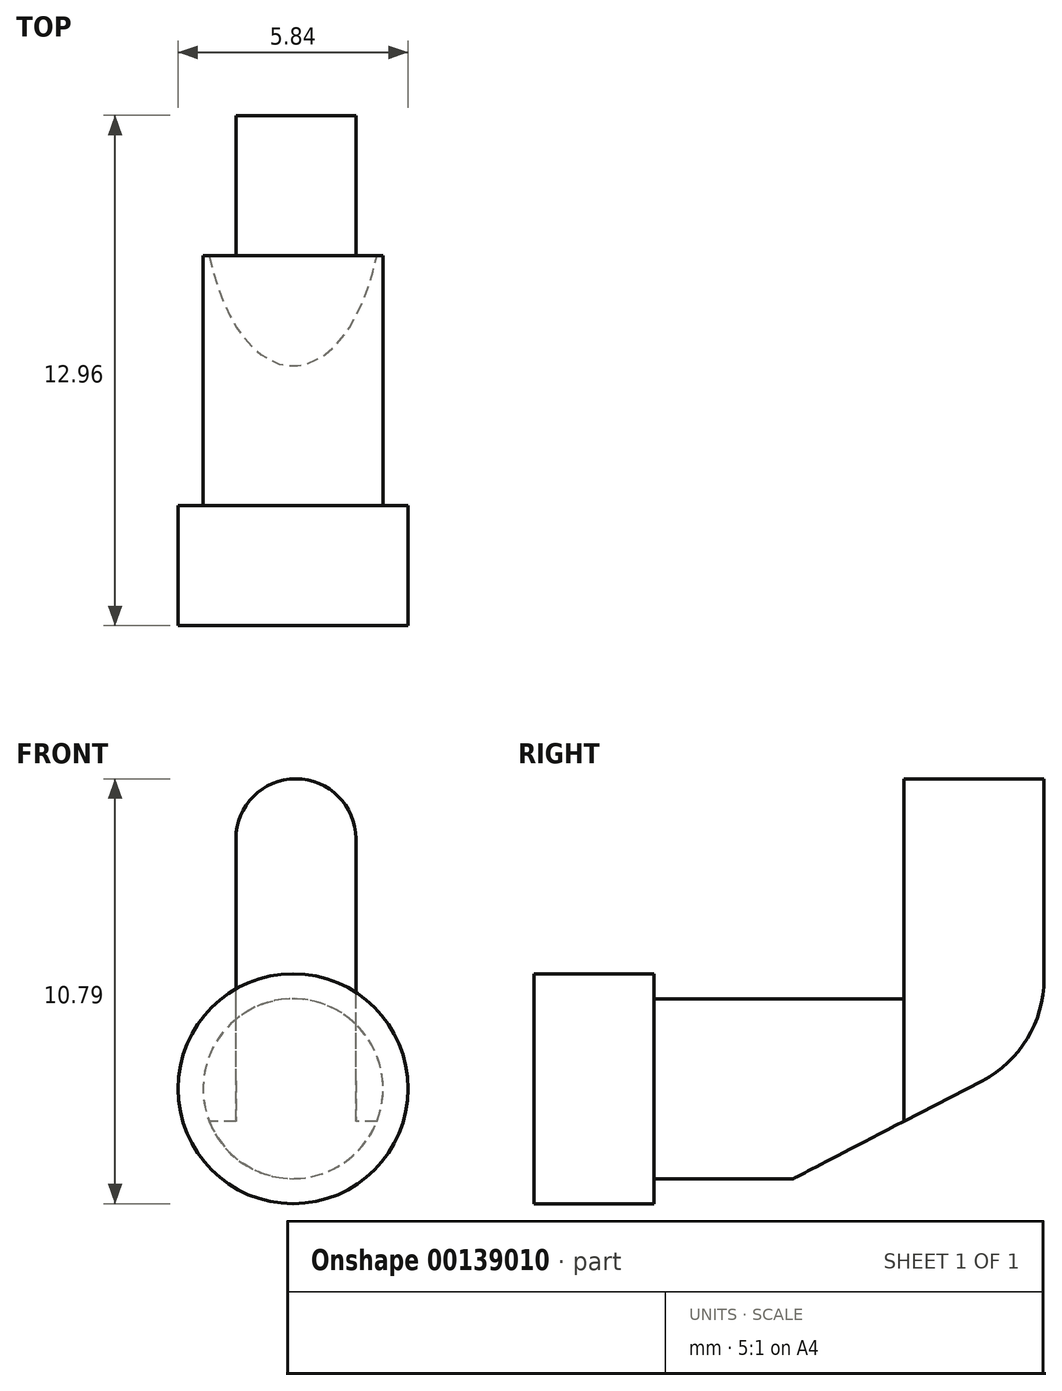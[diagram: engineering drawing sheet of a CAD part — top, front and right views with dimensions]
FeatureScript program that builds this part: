
annotation { "Feature Type Name" : "Feature", "Feature Type Description" : "" }
export const myFeature = defineFeature(function(context is Context, id is Id, definition is map)
    precondition{}
    {
        {
            var Q0;
            Q0=qCreatedBy(makeId("Front.planeOp"),FACE);
            var sketch = newSketch(context, id + "F0", { "sketchPlane" : qUnion([Q0])});
            skCircle(sketch, "E0", {"center": v(0, 0) * mm, "radius": 2.29 * mm});
            skSolve(sketch);
        }
        {
            var Q0;
            Q0 = qSketchRegion(id + "F0", true);
            extrude(context, id + "F1", {"entities" : qUnion([Q0]), "depth" : 6.35 * mm});
        }
        {
            var Q0;
            Q0=makeQuery(id+"F1.opExtrude","CAP_FACE",FACE,{"disambiguationData":[OSD([sQuery(id+"F0.wireOp",EDGE,"E0")])],"isStart":false});
            var sketch = newSketch(context, id + "F2", { "sketchPlane" : qUnion([Q0])});
            skCircle(sketch, "E1", {"center": v(0, 0) * mm, "radius": 2.92 * mm});
            skSolve(sketch);
        }
        {
            var Q0;
            Q0 = qSketchRegion(id + "F2", true);
            extrude(context, id + "F3", {"entities" : qUnion([Q0]), "operationType" : NewBodyOperationType.ADD, "depth" : 3.05 * mm});
        }
        {
            var Q0;
            Q0=makeQuery(id+"F1.opExtrude","CAP_FACE",FACE,{"disambiguationData":[OSD([sQuery(id+"F0.wireOp",EDGE,"E0")])],"isStart":true});
            var sketch = newSketch(context, id + "F4", { "sketchPlane" : qUnion([Q0])});
            skLineSegment(sketch, "E2", {"start": v(-1.6, 0) * mm, "end": v(-1.6, 6.36) * mm});
            skLineSegment(sketch, "E3", {"start": v(1.45, 0) * mm, "end": v(1.45, 6.35) * mm});
            skLineSegment(sketch, "E4", {"start": v(-1.6, 0) * mm, "end": v(1.45, 0) * mm});
            skArc(sketch, "E5", {"start": v(1.45, 6.35) * mm, "mid": v(-0.07, 7.87) * mm, "end": v(-1.6, 6.36) * mm});
            skSolve(sketch);
        }
        {
            var Q0;
            Q0 = qSketchRegion(id + "F4", true);
            extrude(context, id + "F5", {"entities" : qUnion([Q0]), "operationType" : NewBodyOperationType.ADD, "depth" : 3.56 * mm});
        }
        {
            var Q0;
            Q0=makeQuery(id+"F5.opExtrude","SWEPT_FACE",FACE,{"disambiguationData":[OSD([sQuery(id+"F4.wireOp",EDGE,"E2")])]});
            var sketch = newSketch(context, id + "F6", { "sketchPlane" : qUnion([Q0])});
            skFitSpline(sketch, "E6", {"points": [v(3.56, 0) * mm, v(0, -1.3) * mm], "startDerivative": vector(0.31, -3.55) * mm, "endDerivative": vector(-10.98, -0.34) * mm});
            skLineSegment(sketch, "E7", {"start": v(0, -1.3) * mm, "end": v(0, 0) * mm});
            skLineSegment(sketch, "E8", {"start": v(0, 0) * mm, "end": v(3.56, 0) * mm});
            skSolve(sketch);
        }
        {
            var Q0;
            Q0=makeQuery(id+"F6.imprint","IMPRINT",FACE,{"disambiguationData":[TD([[makeQuery(id+"F6.imprint","IMPRINT",EDGE,{"derivedFrom":sQuery(id+"F6.wireOp",EDGE,"E6")}),-1.0]])]});
            extrude(context, id + "F7", {"entities" : qUnion([Q0]), "operationType" : NewBodyOperationType.ADD, "oppositeDirection" : true, "depth" : 3.05 * mm});
        }
        {
            var Q0;
            Q0=qCreatedBy(makeId("Right.planeOp"),FACE);
            var sketch = newSketch(context, id + "F8", { "sketchPlane" : qUnion([Q0])});
            skFitSpline(sketch, "E9", {"points": [v(-3.13, -2.45) * mm, v(3.51, 1) * mm], "startDerivative": vector(21.48, -3.7) * mm, "endDerivative": vector(-4.82, 2.99) * mm});
            skLineSegment(sketch, "E10", {"start": v(-3.13, -2.45) * mm, "end": v(3.51, 1) * mm});
            skSolve(sketch);
        }
        {
            var Q0;
            Q0 = qSketchRegion(id + "F8", true);
            extrude(context, id + "F9", {"entities" : qUnion([Q0]), "operationType" : NewBodyOperationType.REMOVE, "depth" : 45.02 * mm, "hasSecondDirection" : true, "secondDirectionOppositeDirection" : true, "secondDirectionDepth" : 29.97 * mm});
        }
        {
            var Q0;
            Q0=makeQuery(id+"F9.boolean.opBoolean","INTERSECT",EDGE,{"derivedFrom":[makeQuery(id+"F5.opExtrude","CAP_FACE",FACE,{"disambiguationData":[OSD([sQuery(id+"F4.wireOp",EDGE,"E2"),sQuery(id+"F4.wireOp",EDGE,"E3"),sQuery(id+"F4.wireOp",EDGE,"E4"),sQuery(id+"F4.wireOp",EDGE,"E5")])],"isStart":false}),makeQuery(id+"F9.opExtrude","SWEPT_FACE",FACE,{"disambiguationData":[OSD([sQuery(id+"F8.wireOp",EDGE,"E9")])]})]});
            fillet(context, id + "F10", {"entities" : qUnion([Q0]), "radius" : 6.5 * mm, "tangentPropagation" : true, "allowEdgeOverflow" : false});
        }
        {
            var Q0;
            Q0=makeQuery(id+"F10.opFillet","BLEND_EDGE",EDGE,{"blendedFrom":[makeQuery(id+"F9.boolean.opBoolean","INTERSECT",EDGE,{"derivedFrom":[makeQuery(id+"F5.opExtrude","CAP_FACE",FACE,{"disambiguationData":[OSD([sQuery(id+"F4.wireOp",EDGE,"E2"),sQuery(id+"F4.wireOp",EDGE,"E3"),sQuery(id+"F4.wireOp",EDGE,"E4"),sQuery(id+"F4.wireOp",EDGE,"E5")])],"isStart":false}),makeQuery(id+"F9.opExtrude","SWEPT_FACE",FACE,{"disambiguationData":[OSD([sQuery(id+"F8.wireOp",EDGE,"E9")])]})]}),makeQuery(id+"F9.boolean.opBoolean","COPY",FACE,{"derivedFrom":makeQuery(id+"F9.opExtrude","SWEPT_FACE",FACE,{"disambiguationData":[OSD([sQuery(id+"F8.wireOp",EDGE,"E10")])]})})],"blendedInto":[makeQuery(id+"F9.boolean.opBoolean","COPY",FACE,{"derivedFrom":makeQuery(id+"F9.opExtrude","SWEPT_FACE",FACE,{"disambiguationData":[OSD([sQuery(id+"F8.wireOp",EDGE,"E10")])]})})]});
            fillet(context, id + "F11", {"entities" : qUnion([Q0]), "radius" : 2.9 * mm, "tangentPropagation" : true, "allowEdgeOverflow" : false});
        }
    });
